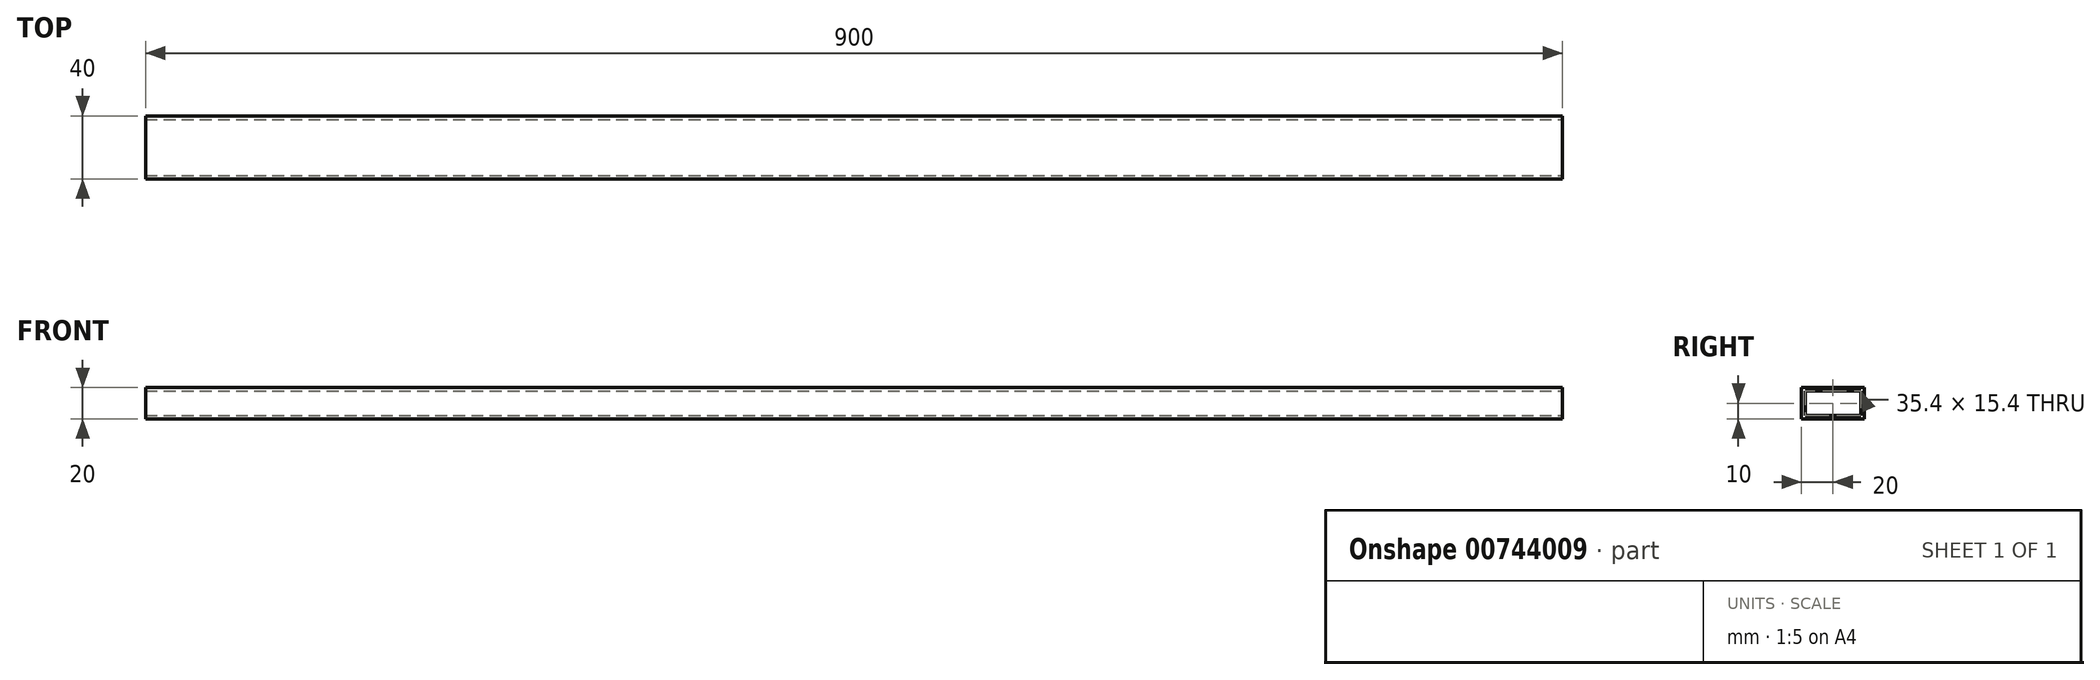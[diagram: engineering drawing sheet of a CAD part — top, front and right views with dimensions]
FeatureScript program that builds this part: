
annotation { "Feature Type Name" : "Feature", "Feature Type Description" : "" }
export const myFeature = defineFeature(function(context is Context, id is Id, definition is map)
    precondition{}
    {
        {
            var Q0;
            Q0=qCreatedBy(makeId("Right.planeOp"),FACE);
            var sketch = newSketch(context, id + "F0", { "sketchPlane" : qUnion([Q0])});
            skLineSegment(sketch, "E0.bottom", {"start": v(20, 10) * mm, "end": v(-20, 10) * mm});
            skLineSegment(sketch, "E0.top", {"start": v(20, -10) * mm, "end": v(-20, -10) * mm});
            skLineSegment(sketch, "E0.left", {"start": v(20, 10) * mm, "end": v(20, -10) * mm});
            skLineSegment(sketch, "E0.right", {"start": v(-20, 10) * mm, "end": v(-20, -10) * mm});
            skPoint(sketch, "E0.middle", {"position": v(0, 0) * mm});
            skLineSegment(sketch, "E1.0", {"start": v(-17.7, 7.7) * mm, "end": v(-17.7, -7.7) * mm});
            skLineSegment(sketch, "E1.1", {"start": v(17.7, 7.7) * mm, "end": v(-17.7, 7.7) * mm});
            skLineSegment(sketch, "E1.2", {"start": v(17.7, 7.7) * mm, "end": v(17.7, -7.7) * mm});
            skLineSegment(sketch, "E1.3", {"start": v(17.7, -7.7) * mm, "end": v(-17.7, -7.7) * mm});
            skSolve(sketch);
        }
        {
            var Q0;
            Q0 = qSketchRegion(id + "F0", true);
            extrude(context, id + "F1", {"entities" : qUnion([Q0]), "oppositeDirection" : true, "depth" : 900 * mm, "offsetDistance" : 25 * mm});
        }
    });
